# Revit family: Faucet-Bedpan_Washer-Zurn-Z85500-XL-WM-EVB-HK-SE-SH-VC
name_source: partatom
category: Plumbing Fixtures
units: mm (PartAtom-declared; Revit-internal decimal feet)

## family parameters
Cut with Voids When Loaded = No
Host = Face
Maintain Annotation Orientation = No
OmniClass Number = 23.45.55.17
OmniClass Title = Mixing Faucets
Part Type = Normal
Room Calculation Point = No
Round Connector Dimension = Use Radius
Shared = No

## types (1)
- Z85500-WM-EVB-HK-SE-SH-VC Bedpan Washer
    Activation Method = Manual Operated
    Assembly Code = D2010.60
    CW Connection = Yes
    CWFU = 1
    Default Elevation = 48 "
    Description = AquaSpec® lead-free bedpan washer
    Distance Between Hot  & Cold water Axis Inlet = 2.5 "
    Distance b/w Ground & Food Pedals = 2 "
    Distance between Wall and Spray Hose Center = 2.875 "
    HW Connection = Yes
    HWFU = 1
    Inlet Axis of Water to Ground = 13 "
    Inlet Connection Size (inch) = 1 "
    Main Material = Chrome-Plated Brass - Zurn - Polished
    Manufacturer = Zurn Water, LLC
    Manufacturer Brand = Zurn
    Model = Z85500-XL-WM-EVB-HK-SE-SH-VC
    Modified Date = 02/13/2026
    Product Documentation Link = https://files.zurn.com
    Product Installation Sheet URL = https://files.zurn.com
    Product Page URL = https://www.zurn.com
    Product data URL = https://www.bimobject.com
    Repair Parts URL = https://files.zurn.com
    Spray Hose Mounting Height from Floor = 66 "
    URL = www.zurn.com
    Vent Connection = No
    WFU = 0
    Waste Connection = No
    Width of Valve = 5 "
    Width of assembly = 13.875 "

## geometry (parser evidence)
native form markers: Sweep x17
no freeform markers — native parametric forms only
